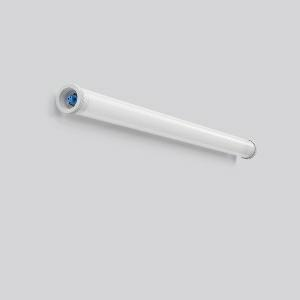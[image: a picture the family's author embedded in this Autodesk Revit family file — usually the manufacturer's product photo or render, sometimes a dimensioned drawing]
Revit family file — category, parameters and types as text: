
# Revit family: planox_tube_601071_002_1_646b
name_source: partatom
category: Lighting Fixtures
units: mm (PartAtom-declared; Revit-internal decimal feet)

## family parameters
Cut with Voids When Loaded = No
Host = Face
Light Source = No
Part Type = Normal
Room Calculation Point = No
Round Connector Dimension = Use Diameter
Shared = No

## types (1)
- PLANOX TUBE (1 x LED Modul 840, 5350 lm, 4000)
    Apparent Load = 39 VA
    CIE Flux Codes = 42 71 89 90 100
    Color Rendering = 80
    Color Temperature = 4000
    Default Elevation = 1800 mm
    Description = Series: PLANOX TUBE
Robust protective tube luminaire for tough requirements. Rack made of sheet steel, white powder coated. End caps made of plastic (polyamide) grey. Diffuser made of plastic (polycarbonate), opal, shockproof. Symmetrical light distribution. Homogeneous light distribution. With accessories for wall, ceiling or pendant mounting. Driver integrated. Easy installation with the Plug+Play Wieland RST CLASSIC plug-in system. Luminaire with integrated through-wiring for series connection of further luminaires by two Wieland RST Classic plug connectors (plug and socket). Accessories for electrical connection must be ordered separately. Mounting set must be ordered separately. Luminaire with limited surface temperature in accordance with EN 60598-2-24 for use in environments in which a deposit of conductive dust on the luminaire can be expected. Qualified for use in the food and drink industry. Suitable for lighting in public car parks and public off-street parking spaces according to DIN 67528. Environmentally friendly and resource-saving due to replaceable components. 
Colour: white
Diameter: 78 mm
Length: 1280 mm
Lamp: LED
Socket: without socket
Colour temperature: 4000K
Colour rendering index (CRI): 83
System power: 39 W
Rated luminous flux: 5350 lm
Luminous efficiency: 137 lm/W
Control gear: Regulated power supply
Protection class: I
Type of protection: IP 67
    Height = 0 mm  [stored 0 ft]
    Lamp = 1 x LED Modul 840
    Lamp Light Flux = 5350 lm
    Lamp count = 1
    Length = 1280 mm
    Lifetime = 50000 h
    Luminous efficacy = 137 lm/W
    Manufacturer = RZB
    ModVariant = No
    Model = 601071.002.1
    Mounting Place = Ceiling
    Mounting Type = Surface mounted
    Number of Poles = 1
    OnlyDefault = Yes
    Power Factor = 1
    Product Name = PLANOX TUBE
    Product group = Surface mounted luminaires for moist/humid enviroments
    ProductGroupID = 308
    Protection Class = Protection class I
    Protection Degree = Degree of protection
    RLX_Detail_Level = 1
    RLX_Emergency_Light_Flux = 0 lm
    RLX_Emergency_Type = 0
    RLX_Emergency_Type_DB = No
    RlxData = <blob elided: 34049 chars, md5=7ed145a5>
    Socket = socket
    Standby Power = 0 W
    System Light Flux = 5350 lm
    System Power = 39 W
    Type Comments = Product without accessories
    Type Image = 601071.002.jpg
    URL = http://relux.com
    VarID = ---
    Voltage = 0 V
    Weight = 0.00 kg
    Width = 0 mm  [stored 0 ft]

note: [stored X ft] marks values corroborated as IEEE doubles in the binary element streams (Revit-internal decimal feet)

## geometry (parser evidence)
native form markers: Blend x4, Sweep x12
no freeform markers — native parametric forms only
